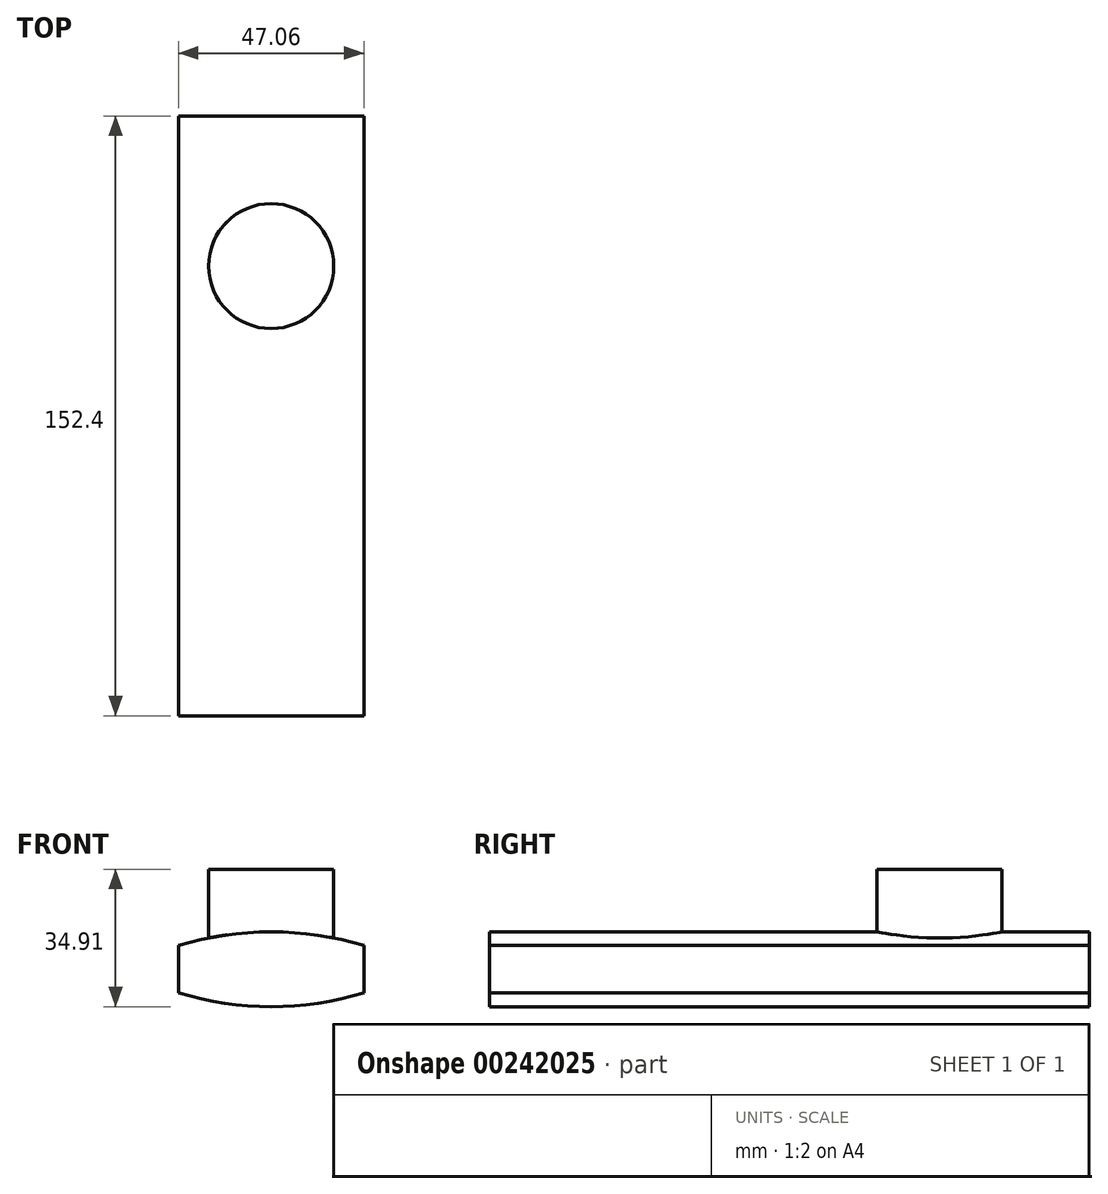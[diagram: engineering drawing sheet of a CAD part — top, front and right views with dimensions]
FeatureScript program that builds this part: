
annotation { "Feature Type Name" : "Feature", "Feature Type Description" : "" }
export const myFeature = defineFeature(function(context is Context, id is Id, definition is map)
    precondition{}
    {
        {
            var Q0;
            Q0=qCreatedBy(makeId("Front.planeOp"),FACE);
            var sketch = newSketch(context, id + "F0", { "sketchPlane" : qUnion([Q0])});
            skLineSegment(sketch, "E0", {"start": v(-23.53, 6) * mm, "end": v(-23.53, -6) * mm});
            skLineSegment(sketch, "E1.MirrorCS", {"start": v(23.53, 6) * mm, "end": v(23.53, -6) * mm});
            skArc(sketch, "E2", {"start": v(23.53, 6) * mm, "mid": v(0, 9.5) * mm, "end": v(-23.53, 6) * mm});
            skArc(sketch, "E3.MirrorCS", {"start": v(23.53, -6) * mm, "mid": v(0, -9.5) * mm, "end": v(-23.53, -6) * mm});
            skSolve(sketch);
        }
        {
            var Q0;
            Q0 = qSketchRegion(id + "F0", true);
            extrude(context, id + "F1", {"entities" : qUnion([Q0]), "endBound" : BoundingType.SYMMETRIC, "depth" : 152.4 * mm});
        }
        {
            var Q0;
            Q0=qCreatedBy(makeId("Top.planeOp"),FACE);
            var sketch = newSketch(context, id + "F2", { "sketchPlane" : qUnion([Q0])});
            skCircle(sketch, "E4", {"center": v(0, 38.05) * mm, "radius": 15.9 * mm});
            skSolve(sketch);
        }
        {
            var Q0;
            Q0 = qSketchRegion(id + "F2", true);
            extrude(context, id + "F3", {"entities" : qUnion([Q0]), "operationType" : NewBodyOperationType.ADD, "depth" : 25.4 * mm});
        }
    });
